# Revit family: Toilet_Seat-Round-American_Standard-Cardiff-5259B65MT_Series
name_source: partatom
category: Specialty Equipment
revit_build: Autodesk Revit 2018 (Build: 20170223_1515(x64)
units: mm (PartAtom-declared; Revit-internal decimal feet)

## family parameters
Always vertical = No
Cut with Voids When Loaded = No
OmniClass Number = 23.45.00.00
OmniClass Title = Sanitary, Laundry, and Cleaning Equipment
Part Type = Normal
Room Calculation Point = No
Round Connector Dimension = Use Diameter
Shared = Yes
Work Plane-Based = Yes

## types (3) — shared parameters
Assembly Code = C1030200
Default Elevation = 0"
Description = Cardiff Round Front Slow-Close Toilet Seat
Height = 1 1/2"
Installation Type = Surface Mounted
Length = 15 3/8"
Manufacturer = American Standard
Price = Prices may vary. Please consult Manufacturer Representative for most up-to-date price list.
Product Documentation Link = https://www.americanstandard-us.com
Product Page URL = https://www.americanstandard-us.com
URL = http://www.americanstandard-us.com
Warranty Information = 1 Year Limited Warranty
Width = 14 3/16"

## per-type parameters (varying)
| type | Finish | Material |
| 5259B65MT.020 | Plastic-American Standard-020-White | Plastic-American Standard-020-White |
| 5259B65MT.021 | Plastic-American Standard-021-Bone | Plastic-American Standard-021-Bone |
| 5259B65MT.222 | Plastic-American Srandard-222-Linen | Plastic-American Srandard-222-Linen |

note: column(s) folded — value = type name in every type: Model

## geometry (parser evidence)
native form markers: Sweep x2
no freeform markers — native parametric forms only
